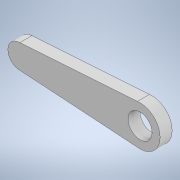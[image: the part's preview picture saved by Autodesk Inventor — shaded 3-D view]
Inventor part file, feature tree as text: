
AUTODESK INVENTOR PART (.ipt)
format: ipt  version: 2020.3 (Build 243373000, 373)  size: 105,472 bytes
history: native  units: mm
features: extrude x1, direct_edit x1, sketch x1, move_body x1
ambient origin geometry x8: Origin, YZ Plane, XZ Plane, XY Plane, X Axis, Y Axis, Z Axis, Center Point
bodies: Solid1 (feature_tree)
feature tree (4):
  extrude  "Extrusion1"  Depth=10.0mm
  direct_edit  "Direct Edit1"
  sketch  "Sketch1"  dims[d0=6.0mm d1=10.0mm d2=6.0mm d3=3.0mm d4=0.0mm d5=0.0mm d6=0.0mm d7=15.25mm]
  move_body  "Move1"
